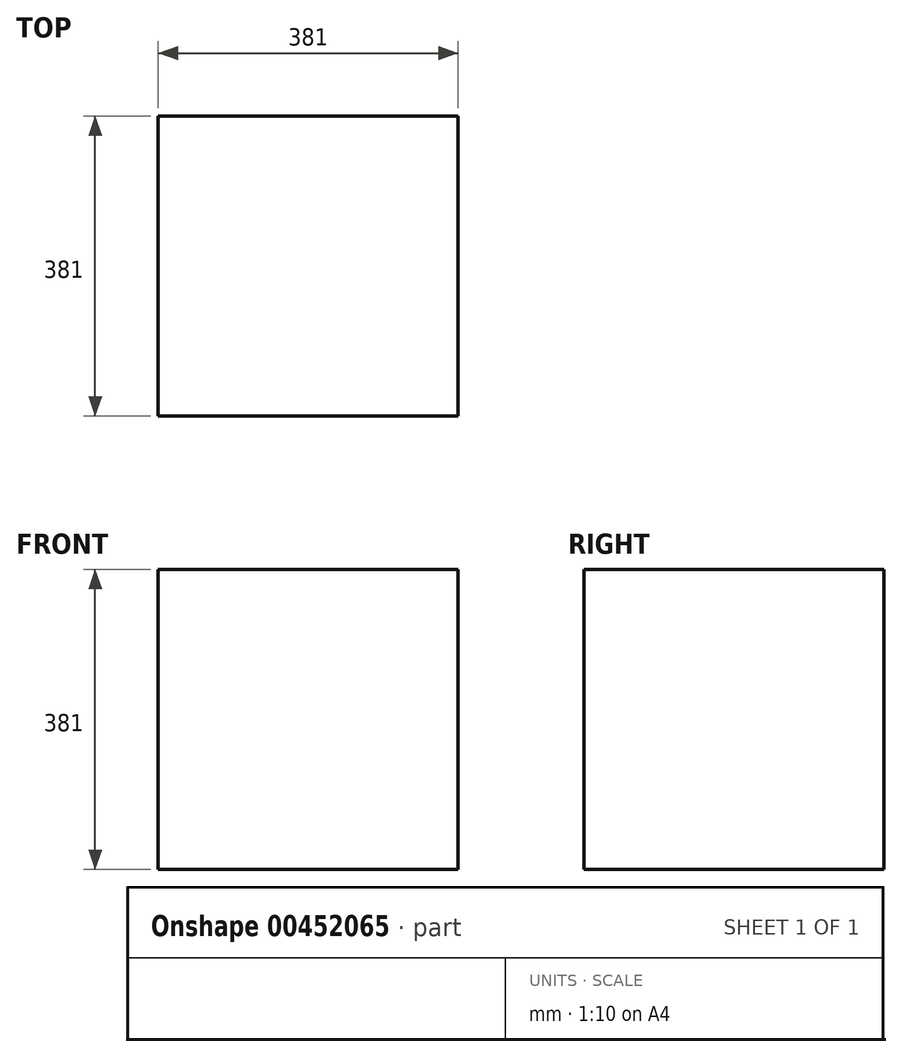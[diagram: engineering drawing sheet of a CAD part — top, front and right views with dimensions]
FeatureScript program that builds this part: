
annotation { "Feature Type Name" : "Feature", "Feature Type Description" : "" }
export const myFeature = defineFeature(function(context is Context, id is Id, definition is map)
    precondition{}
    {
        {
            var Q0;
            Q0=qCreatedBy(makeId("Top.planeOp"),FACE);
            var sketch = newSketch(context, id + "F0", { "sketchPlane" : qUnion([Q0])});
            skLineSegment(sketch, "E0.bottom", {"start": v(-190.5, 190.5) * mm, "end": v(190.5, 190.5) * mm});
            skLineSegment(sketch, "E0.top", {"start": v(-190.5, -190.5) * mm, "end": v(190.5, -190.5) * mm});
            skLineSegment(sketch, "E0.left", {"start": v(-190.5, 190.5) * mm, "end": v(-190.5, -190.5) * mm});
            skLineSegment(sketch, "E0.right", {"start": v(190.5, 190.5) * mm, "end": v(190.5, -190.5) * mm});
            skSolve(sketch);
        }
        {
            var Q0;
            Q0=makeQuery(id+"F0.imprint","IMPRINT",FACE,{"disambiguationData":[TD([[makeQuery(id+"F0.imprint","IMPRINT",EDGE,{"derivedFrom":sQuery(id+"F0.wireOp",EDGE,"E0.bottom")}),-1.0]])]});
            extrude(context, id + "F1", {"entities" : qUnion([Q0]), "depth" : 381 * mm});
        }
    });
